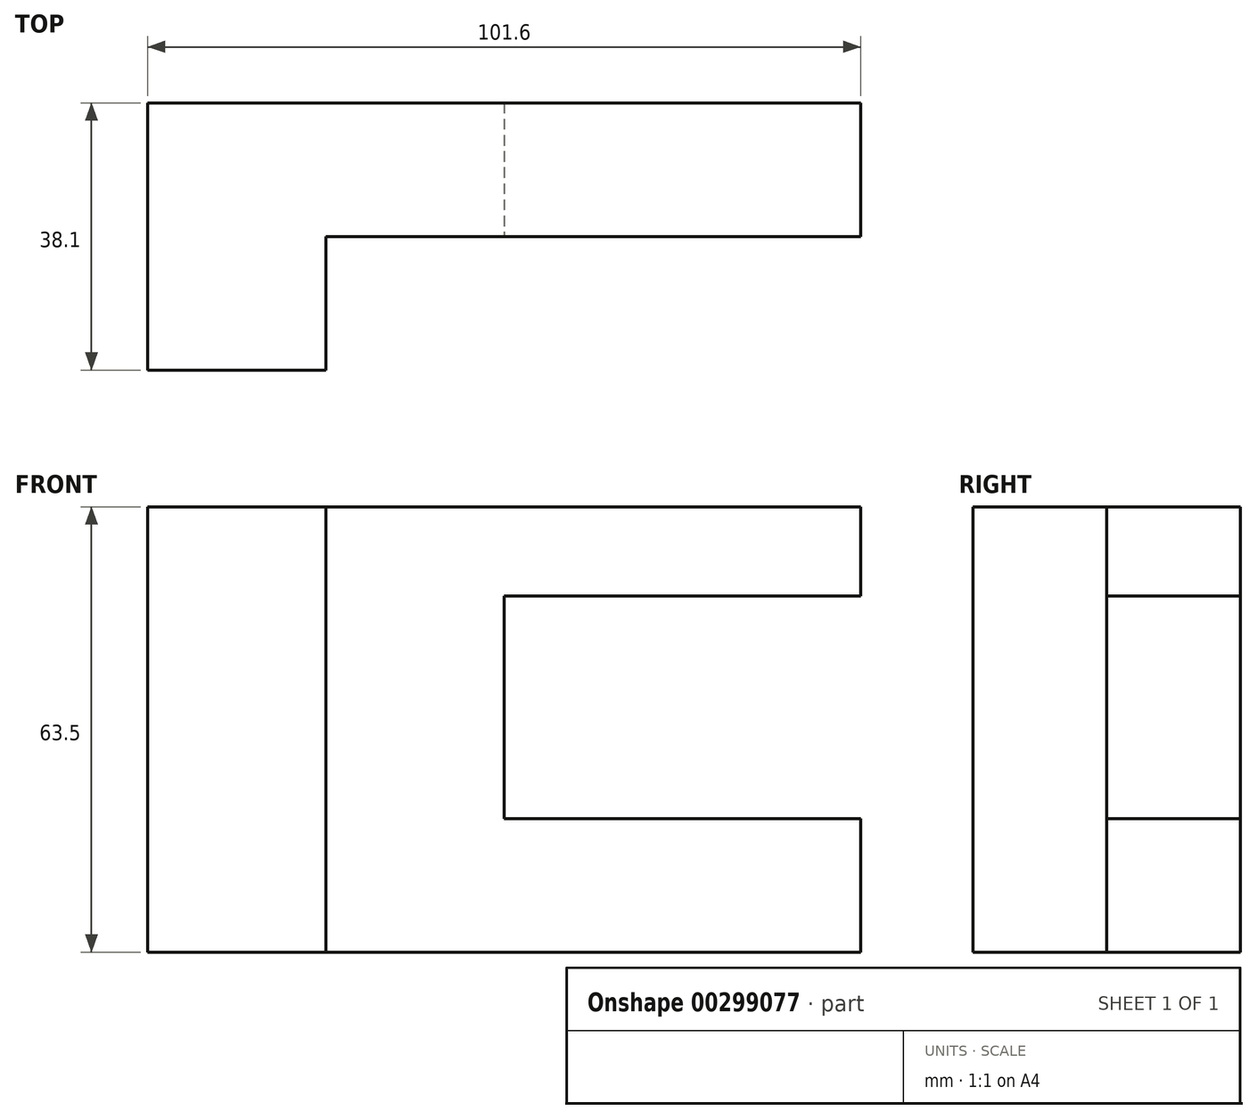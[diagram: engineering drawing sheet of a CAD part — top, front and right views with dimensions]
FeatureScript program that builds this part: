
annotation { "Feature Type Name" : "Feature", "Feature Type Description" : "" }
export const myFeature = defineFeature(function(context is Context, id is Id, definition is map)
    precondition{}
    {
        {
            var Q0;
            Q0=qCreatedBy(makeId("Front.planeOp"),FACE);
            var sketch = newSketch(context, id + "F0", { "sketchPlane" : qUnion([Q0])});
            skLineSegment(sketch, "E0.bottom", {"start": v(50.8, -31.75) * mm, "end": v(-50.8, -31.75) * mm});
            skLineSegment(sketch, "E0.top", {"start": v(50.8, 31.75) * mm, "end": v(-50.8, 31.75) * mm});
            skLineSegment(sketch, "E0.left", {"start": v(50.8, -31.75) * mm, "end": v(50.8, 31.75) * mm});
            skLineSegment(sketch, "E0.right", {"start": v(-50.8, -31.75) * mm, "end": v(-50.8, 31.75) * mm});
            skPoint(sketch, "E0.middle", {"position": v(0, 0) * mm});
            skSolve(sketch);
        }
        {
            var Q0;
            Q0 = qSketchRegion(id + "F0", true);
            extrude(context, id + "F1", {"entities" : qUnion([Q0]), "depth" : 19.05 * mm});
        }
        {
            var Q0;
            Q0=makeQuery(id+"F1.opExtrude","CAP_FACE",FACE,{"disambiguationData":[OSD([sQuery(id+"F0.wireOp",EDGE,"E0.bottom"),sQuery(id+"F0.wireOp",EDGE,"E0.top"),sQuery(id+"F0.wireOp",EDGE,"E0.left"),sQuery(id+"F0.wireOp",EDGE,"E0.right")])],"isStart":false});
            var sketch = newSketch(context, id + "F2", { "sketchPlane" : qUnion([Q0])});
            skLineSegment(sketch, "E1.bottom", {"start": v(50.8, 19.05) * mm, "end": v(0, 19.05) * mm});
            skLineSegment(sketch, "E1.top", {"start": v(50.8, -12.7) * mm, "end": v(0, -12.7) * mm});
            skLineSegment(sketch, "E1.left", {"start": v(50.8, 19.05) * mm, "end": v(50.8, -12.7) * mm});
            skLineSegment(sketch, "E1.right", {"start": v(0, 19.05) * mm, "end": v(0, -12.7) * mm});
            skSolve(sketch);
        }
        {
            var Q0;
            Q0 = qSketchRegion(id + "F2", true);
            extrude(context, id + "F3", {"entities" : qUnion([Q0]), "operationType" : NewBodyOperationType.REMOVE, "endBound" : BoundingType.THROUGH_ALL, "oppositeDirection" : true, "depth" : 38.1 * mm});
        }
        {
            var Q0;
            Q0=makeQuery(id+"F1.opExtrude","CAP_FACE",FACE,{"disambiguationData":[OSD([sQuery(id+"F0.wireOp",EDGE,"E0.bottom"),sQuery(id+"F0.wireOp",EDGE,"E0.top"),sQuery(id+"F0.wireOp",EDGE,"E0.left"),sQuery(id+"F0.wireOp",EDGE,"E0.right")])],"isStart":false});
            var sketch = newSketch(context, id + "F4", { "sketchPlane" : qUnion([Q0])});
            skLineSegment(sketch, "E2.bottom", {"start": v(-50.8, 31.75) * mm, "end": v(-25.4, 31.75) * mm});
            skLineSegment(sketch, "E2.top", {"start": v(-50.8, -31.75) * mm, "end": v(-25.4, -31.75) * mm});
            skLineSegment(sketch, "E2.left", {"start": v(-50.8, 31.75) * mm, "end": v(-50.8, -31.75) * mm});
            skLineSegment(sketch, "E2.right", {"start": v(-25.4, 31.75) * mm, "end": v(-25.4, -31.75) * mm});
            skSolve(sketch);
        }
        {
            var Q0;
            Q0 = qSketchRegion(id + "F4", true);
            extrude(context, id + "F5", {"entities" : qUnion([Q0]), "operationType" : NewBodyOperationType.ADD, "depth" : 19.05 * mm});
        }
    });
